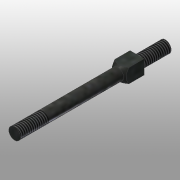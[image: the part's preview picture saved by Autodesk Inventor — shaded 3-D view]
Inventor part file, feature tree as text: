
AUTODESK INVENTOR PART (.ipt)
format: ipt  version: 2015 (Build 190159000, 159)  size: 102,400 bytes
history: native  units: mm
features: sketch x4, other x3
ambient origin geometry x8: Origin, YZ Plane, XZ Plane, XY Plane, X Axis, Y Axis, Z Axis, Center Point
bodies: Solid1 (feature_tree)
feature tree (7):
  other  "500-001.ipt"
  other  "Solid1::500-001.ipt"
  other  "TaggingFeature1"
  sketch  "Sketch1"  dims[d0=10.0mm]
  sketch  "Sketch2"
  sketch  "Sketch3"
  sketch  "Sketch4"
